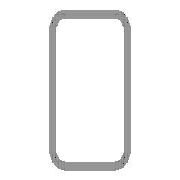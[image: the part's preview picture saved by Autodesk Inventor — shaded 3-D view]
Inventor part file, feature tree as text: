
AUTODESK INVENTOR PART (.ipt)
format: ipt  version: 2025.3 (Build 293356030, 356C)  size: 150,016 bytes
history: native  units: mm (DEFAULTED — no unit token found)
features: other x4, plane x3, split x2, sketch x1
ambient origin geometry x8: Origin, YZ Plane, XZ Plane, XY Plane, X Axis, Y Axis, Z Axis, Center Point
bodies: Solid1 (feature_tree), Body (feature_tree)
feature tree (10):
  parser-record x1  (decoder bookkeeping rows leaked as tree rows — omitted from the tree; the rows remain in map.json)
  other  "Driven Length"
  other  "Start Plane"
  other  "End Plane"
  plane  "Work Plane4"
  split  "Split1"
  plane  "Work Plane5"
  split  "Split2"
  sketch  "Sketch3"  dims[d3=900.038447mm d4=0.0mm d7=6.0mm d9=40.0mm d11=80.0mm d12=3.0mm d13=35.281881mm d14=935.320328mm d15=20.0mm d16=40.0mm d17=90.0deg d18=900.038447mm]
  plane  "Work Plane3"
